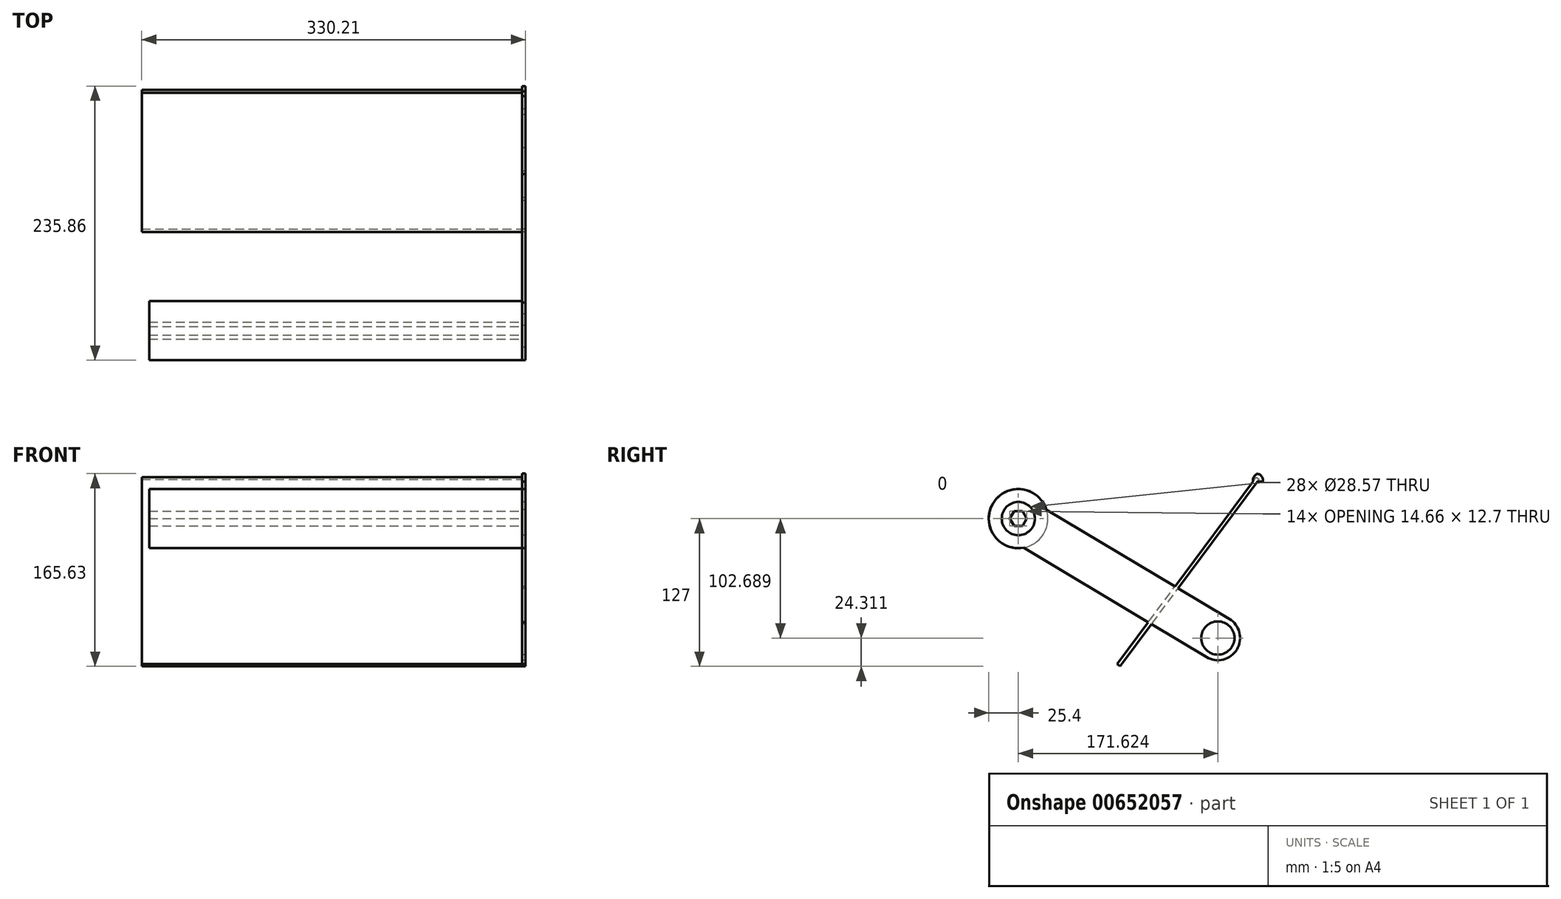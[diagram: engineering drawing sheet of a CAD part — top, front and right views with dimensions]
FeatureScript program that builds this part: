
annotation { "Feature Type Name" : "Feature", "Feature Type Description" : "" }
export const myFeature = defineFeature(function(context is Context, id is Id, definition is map)
    precondition{}
    {
        {
            var Q0;
            Q0=qCreatedBy(makeId("Right.planeOp"),FACE);
            var sketch = newSketch(context, id + "F0", { "sketchPlane" : qUnion([Q0])});
            skCircle(sketch, "E0", {"center": v(0, 0) * mm, "radius": 25.4 * mm});
            skCircle(sketch, "E1.cCircle", {"center": v(0, 0) * mm, "radius": 6.35 * mm, "construction": true});
            skLineSegment(sketch, "E1.0", {"start": v(-3.67, 6.35) * mm, "end": v(3.67, 6.35) * mm});
            skLineSegment(sketch, "E1.1", {"start": v(3.67, 6.35) * mm, "end": v(7.33, 0) * mm});
            skLineSegment(sketch, "E1.2", {"start": v(7.33, 0) * mm, "end": v(3.67, -6.35) * mm});
            skLineSegment(sketch, "E1.3", {"start": v(3.67, -6.35) * mm, "end": v(-3.67, -6.35) * mm});
            skLineSegment(sketch, "E1.4", {"start": v(-3.67, -6.35) * mm, "end": v(-7.33, 0) * mm});
            skLineSegment(sketch, "E1.5", {"start": v(-7.33, 0) * mm, "end": v(-3.67, 6.35) * mm});
            skPoint(sketch, "E1.0.midPoint", {"position": v(0, 6.35) * mm});
            skLineSegment(sketch, "E2", {"start": v(-49, -139.7) * mm, "end": v(133.2, -139.7) * mm, "construction": true});
            skLineSegment(sketch, "E3", {"start": v(87.53, -127) * mm, "end": v(207.28, 33.84) * mm});
            skArc(sketch, "E4", {"start": v(9.8, 16.4) * mm, "mid": v(-16.4, 9.8) * mm, "end": v(-9.8, -16.4) * mm});
            skArc(sketch, "E5", {"start": v(161.82, -119.08) * mm, "mid": v(188.01, -112.5) * mm, "end": v(181.43, -86.3) * mm});
            skCircle(sketch, "E6", {"center": v(171.62, -102.69) * mm, "radius": 25.4 * mm, "construction": true});
            skLineSegment(sketch, "E7", {"start": v(153.66, -120.65) * mm, "end": v(189.58, -84.73) * mm, "construction": true});
            skCircle(sketch, "E8", {"center": v(189.58, -84.73) * mm, "radius": 2.49 * mm});
            skCircle(sketch, "E9", {"center": v(153.66, -120.65) * mm, "radius": 2.49 * mm});
            skCircle(sketch, "E10", {"center": v(171.62, -102.69) * mm, "radius": 14.29 * mm});
            skCircle(sketch, "E11", {"center": v(0, 0) * mm, "radius": 14.29 * mm});
            skLineSegment(sketch, "E12", {"start": v(87.53, -127) * mm, "end": v(137.03, -127) * mm, "construction": true});
            skCircle(sketch, "E13", {"center": v(-179.53, -65.48) * mm, "radius": 63.5 * mm, "construction": true});
            skLineSegment(sketch, "E14", {"start": v(87.53, -127) * mm, "end": v(84.98, -125.1) * mm});
            skLineSegment(sketch, "E15", {"start": v(84.98, -125.1) * mm, "end": v(204.73, 35.73) * mm});
            skLineSegment(sketch, "E16", {"start": v(204.73, 35.73) * mm, "end": v(207.28, 33.84) * mm});
            skLineSegment(sketch, "E17.bottom", {"start": v(-6.35, 31.75) * mm, "end": v(210.46, 31.75) * mm});
            skLineSegment(sketch, "E17.top", {"start": v(-31.75, -131.26) * mm, "end": v(210.46, -131.26) * mm});
            skLineSegment(sketch, "E17.left", {"start": v(-31.75, 6.35) * mm, "end": v(-31.75, -131.26) * mm});
            skLineSegment(sketch, "E17.right", {"start": v(210.46, 31.75) * mm, "end": v(210.46, -131.26) * mm});
            skPoint(sketch, "E17.middle", {"position": v(89.35, -49.76) * mm});
            skPoint(sketch, "E18.visualSharp", {"position": v(-31.75, 31.75) * mm});
            skArc(sketch, "E18.filletArc", {"start": v(-6.35, 31.75) * mm, "mid": v(-24.31, 24.31) * mm, "end": v(-31.75, 6.35) * mm});
            skLineSegment(sketch, "E19", {"start": v(181.43, -86.3) * mm, "end": v(9.8, 16.4) * mm});
            skLineSegment(sketch, "E20", {"start": v(-9.8, -16.4) * mm, "end": v(161.82, -119.08) * mm});
            skLineSegment(sketch, "E21", {"start": v(210.46, 39.1) * mm, "end": v(-6.35, 31.75) * mm});
            skLineSegment(sketch, "E22", {"start": v(210.46, 39.1) * mm, "end": v(210.46, 31.75) * mm});
            skSolve(sketch);
        }
        {
            var Q0;
            Q0=makeQuery(id+"F0.imprint","IMPRINT",FACE,{"disambiguationData":[TD([[makeQuery(id+"F0.imprint","IMPRINT",EDGE,{"derivedFrom":sQuery(id+"F0.wireOp",EDGE,"E0")}),-1.0]])]});
            var Q1;
            Q1=makeQuery(id+"F0.imprint","IMPRINT",FACE,{"disambiguationData":[TD([[makeQuery(id+"F0.imprint","IMPRINT",EDGE,{"derivedFrom":sQuery(id+"F0.wireOp",EDGE,"E0")}),1.0]])]});
            var Q2;
            Q2=makeQuery(id+"F0.imprint","IMPRINT",FACE,{"disambiguationData":[TD([[makeQuery(id+"F0.imprint","IMPRINT",EDGE,{"derivedFrom":sQuery(id+"F0.wireOp",EDGE,"E3")}),1.0]])]});
            var Q3;
            {var subQ1=sQuery(id+"F0.wireOp",EDGE,"E4");Q3=makeQuery(id+"F0.imprint","IMPRINT",FACE,{"disambiguationData":[TD([[makeQuery(id+"F0.imprint","IMPRINT",EDGE,{"derivedFrom":subQ1}),1.0]])]});}
            var Q4;
            Q4=makeQuery(id+"F0.imprint","IMPRINT",FACE,{"disambiguationData":[TD([[makeQuery(id+"F0.imprint","IMPRINT",EDGE,{"derivedFrom":sQuery(id+"F0.wireOp",EDGE,"E8")}),-1.0]])]});
            var Q5;
            Q5=makeQuery(id+"F0.imprint","IMPRINT",FACE,{"disambiguationData":[TD([[makeQuery(id+"F0.imprint","IMPRINT",EDGE,{"derivedFrom":sQuery(id+"F0.wireOp",EDGE,"E10")}),-1.0]])]});
            var Q6;
            {var subQ4=sQuery(id+"F0.wireOp",EDGE,"E16");Q6=makeQuery(id+"F0.imprint","IMPRINT",FACE,{"disambiguationData":[TD([[makeQuery(id+"F0.imprint","IMPRINT",EDGE,{"derivedFrom":subQ4}),1.0]])]});}
            extrude(context, id + "F1", {"entities" : qUnion([Q0, Q1, Q2, Q3, Q4, Q5, Q6]), "depth" : 3.17 * mm, "offsetDistance" : 25.4 * mm});
        }
        {
            var Q0;
            Q0=makeQuery(id+"F0.imprint","IMPRINT",FACE,{"disambiguationData":[TD([[makeQuery(id+"F0.imprint","IMPRINT",EDGE,{"derivedFrom":sQuery(id+"F0.wireOp",EDGE,"E0")}),1.0]])]});
            var Q1;
            Q1=makeQuery(id+"F0.imprint","IMPRINT",FACE,{"disambiguationData":[TD([[makeQuery(id+"F0.imprint","IMPRINT",EDGE,{"derivedFrom":sQuery(id+"F0.wireOp",EDGE,"E1.0")}),1.0]])]});
            var Q2;
            {var subQ1=sQuery(id+"F0.wireOp",EDGE,"E4");Q2=makeQuery(id+"F0.imprint","IMPRINT",FACE,{"disambiguationData":[TD([[makeQuery(id+"F0.imprint","IMPRINT",EDGE,{"derivedFrom":subQ1}),1.0]])]});}
            extrude(context, id + "F2", {"entities" : qUnion([Q0, Q1, Q2]), "oppositeDirection" : true, "depth" : 320.67 * mm, "offsetDistance" : 25.4 * mm});
        }
        {
            var Q0;
            Q0=makeQuery(id+"F0.imprint","IMPRINT",FACE,{"disambiguationData":[TD([[makeQuery(id+"F0.imprint","IMPRINT",EDGE,{"derivedFrom":sQuery(id+"F0.wireOp",EDGE,"E3")}),1.0]])]});
            extrude(context, id + "F3", {"entities" : qUnion([Q0]), "oppositeDirection" : true, "depth" : 327.02 * mm, "offsetDistance" : 25.4 * mm});
        }
        {
            var Q0;
            Q0 = qSketchRegion(id + "F0", true);
            var Q1;
            Q1=sQuery(id+"F0.wireOp",EDGE,"E19");
            var Q2;
            Q2=sQuery(id+"F0.wireOp",EDGE,"E20");
            var Q3;
            Q3=sQuery(id+"F0.wireOp",EDGE,"E5");
            var Q4;
            Q4=sQuery(id+"F0.wireOp",EDGE,"E4");
            extrude(context, id + "F4", {"entities" : qUnion([Q0]), "bodyType" : ExtendedToolBodyType.SURFACE, "surfaceEntities" : qUnion([Q1, Q2, Q3, Q4]), "depth" : 15 * mm, "offsetDistance" : 25.4 * mm});
        }
        {
            var Q0;
            Q0=makeQuery(id+"F1.opExtrude","SWEPT_EDGE",EDGE,{"disambiguationData":[OSD([sQuery(id+"F0.wireOp",EDGE,"E17.right"),sQuery(id+"F0.wireOp",EDGE,"E21")])]});
            var Q1;
            Q1=makeQuery(id+"F1.opExtrude","SWEPT_EDGE",EDGE,{"disambiguationData":[OSD([sQuery(id+"F0.wireOp",EDGE,"E17.bottom"),sQuery(id+"F0.wireOp",EDGE,"E21")])]});
            fillet(context, id + "F5", {"entities" : qUnion([Q0, Q1]), "radius" : 6.35 * mm, "tangentPropagation" : true, "allowEdgeOverflow" : false});
        }
    });
